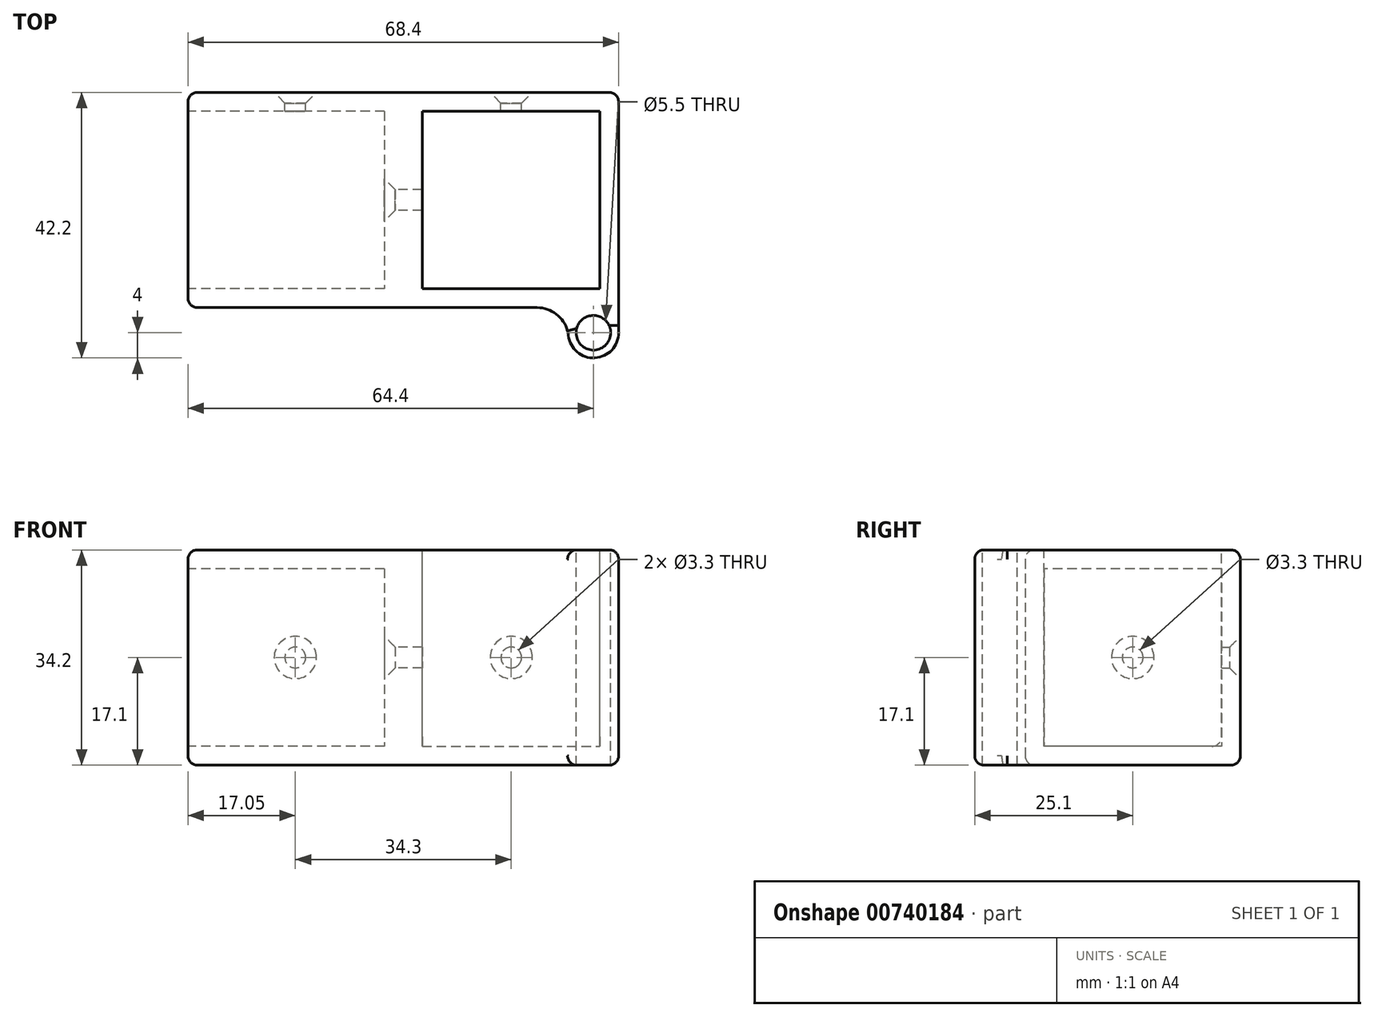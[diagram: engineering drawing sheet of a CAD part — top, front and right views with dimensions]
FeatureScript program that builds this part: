
annotation { "Feature Type Name" : "Feature", "Feature Type Description" : "" }
export const myFeature = defineFeature(function(context is Context, id is Id, definition is map)
    precondition{}
    {
        {
            var Q0;
            Q0=qCreatedBy(makeId("Top.planeOp"),FACE);
            var sketch = newSketch(context, id + "F0", { "sketchPlane" : qUnion([Q0])});
            skLineSegment(sketch, "E0.bottom", {"start": v(-8, 0) * mm, "end": v(-34.2, 0) * mm});
            skLineSegment(sketch, "E0.top", {"start": v(0, 34.2) * mm, "end": v(-34.2, 34.2) * mm});
            skLineSegment(sketch, "E0.left", {"start": v(0, 0) * mm, "end": v(0, 34.2) * mm});
            skLineSegment(sketch, "E0.right", {"start": v(-34.2, 0) * mm, "end": v(-34.2, 34.2) * mm});
            skArc(sketch, "E1", {"start": v(-8, -4) * mm, "mid": v(-4, -8) * mm, "end": v(0, -4) * mm});
            skLineSegment(sketch, "E2", {"start": v(0, 0) * mm, "end": v(0, -4) * mm});
            skLineSegment(sketch, "E3", {"start": v(-8, 0) * mm, "end": v(-8, -4) * mm});
            skLineSegment(sketch, "E4", {"start": v(0, 0) * mm, "end": v(-8, 0) * mm});
            skSolve(sketch);
        }
        {
            var Q0;
            Q0=makeQuery(id+"F0.imprint","IMPRINT",FACE,{"disambiguationData":[TD([[makeQuery(id+"F0.imprint","IMPRINT",EDGE,{"derivedFrom":sQuery(id+"F0.wireOp",EDGE,"E0.bottom")}),-1.0]])]});
            var Q1;
            Q1=makeQuery(id+"F0.imprint","IMPRINT",FACE,{"disambiguationData":[TD([[makeQuery(id+"F0.imprint","IMPRINT",EDGE,{"derivedFrom":sQuery(id+"F0.wireOp",EDGE,"E1")}),1.0]])]});
            extrude(context, id + "F1", {"entities" : qUnion([Q0, Q1]), "depth" : 34.2 * mm, "offsetDistance" : 25 * mm});
        }
        {
            var Q0;
            Q0=makeQuery(id+"F1.opExtrude","CAP_FACE",FACE,{"disambiguationData":[OSD([sQuery(id+"F0.wireOp",EDGE,"E0.bottom"),sQuery(id+"F0.wireOp",EDGE,"E0.top"),sQuery(id+"F0.wireOp",EDGE,"E0.left"),sQuery(id+"F0.wireOp",EDGE,"E0.right"),sQuery(id+"F0.wireOp",EDGE,"E1"),sQuery(id+"F0.wireOp",EDGE,"6FfksXsB-Y7vq-xAn0-bQFg-GBrETYwM94Cl"),sQuery(id+"F0.wireOp",EDGE,"E2"),sQuery(id+"F0.wireOp",EDGE,"E3")])],"isStart":false});
            var sketch = newSketch(context, id + "F2", { "sketchPlane" : qUnion([Q0])});
            skLineSegment(sketch, "E5.bottom", {"start": v(-34.2, 34.2) * mm, "end": v(0, 34.2) * mm});
            skLineSegment(sketch, "E5.top", {"start": v(-34.2, 0) * mm, "end": v(0, 0) * mm});
            skLineSegment(sketch, "E5.left", {"start": v(-34.2, 34.2) * mm, "end": v(-34.2, 0) * mm});
            skLineSegment(sketch, "E5.right", {"start": v(0, 34.2) * mm, "end": v(0, 0) * mm});
            skLineSegment(sketch, "E6.0", {"start": v(-31.2, 31.2) * mm, "end": v(-3, 31.2) * mm});
            skLineSegment(sketch, "E6.1", {"start": v(-31.2, 31.2) * mm, "end": v(-31.2, 3) * mm});
            skLineSegment(sketch, "E6.2", {"start": v(-31.2, 3) * mm, "end": v(-3, 3) * mm});
            skLineSegment(sketch, "E6.3", {"start": v(-3, 31.2) * mm, "end": v(-3, 3) * mm});
            skSolve(sketch);
        }
        {
            var Q0;
            Q0=makeQuery(id+"F2.imprint","IMPRINT",FACE,{"disambiguationData":[TD([[makeQuery(id+"F2.imprint","IMPRINT",EDGE,{"derivedFrom":sQuery(id+"F2.wireOp",EDGE,"E6.0")}),-1.0]])]});
            extrude(context, id + "F3", {"entities" : qUnion([Q0]), "operationType" : NewBodyOperationType.REMOVE, "oppositeDirection" : true, "depth" : 31.2 * mm, "offsetDistance" : 25 * mm});
        }
        {
            var Q0;
            Q0=makeQuery(id+"F1.opExtrude","SWEPT_FACE",FACE,{"disambiguationData":[OSD([sQuery(id+"F0.wireOp",EDGE,"E0.right")])]});
            var sketch = newSketch(context, id + "F4", { "sketchPlane" : qUnion([Q0])});
            skLineSegment(sketch, "E7.bottom", {"start": v(-34.2, 0) * mm, "end": v(0, 0) * mm});
            skLineSegment(sketch, "E7.top", {"start": v(-34.2, 34.2) * mm, "end": v(0, 34.2) * mm});
            skLineSegment(sketch, "E7.left", {"start": v(-34.2, 0) * mm, "end": v(-34.2, 34.2) * mm});
            skLineSegment(sketch, "E7.right", {"start": v(0, 0) * mm, "end": v(0, 34.2) * mm});
            skSolve(sketch);
        }
        {
            var Q0;
            Q0 = qSketchRegion(id + "F4", true);
            extrude(context, id + "F5", {"entities" : qUnion([Q0]), "operationType" : NewBodyOperationType.ADD, "depth" : 34.2 * mm, "offsetDistance" : 25 * mm});
        }
        {
            var Q0;
            Q0=makeQuery(id+"F5.opExtrude","CAP_FACE",FACE,{"disambiguationData":[OSD([sQuery(id+"F4.wireOp",EDGE,"E7.bottom"),sQuery(id+"F4.wireOp",EDGE,"E7.top"),sQuery(id+"F4.wireOp",EDGE,"E7.left"),sQuery(id+"F4.wireOp",EDGE,"E7.right")])],"isStart":false});
            var sketch = newSketch(context, id + "F6", { "sketchPlane" : qUnion([Q0])});
            skLineSegment(sketch, "E8.bottom", {"start": v(-34.2, 34.2) * mm, "end": v(0, 34.2) * mm});
            skLineSegment(sketch, "E8.top", {"start": v(-34.2, 0) * mm, "end": v(0, 0) * mm});
            skLineSegment(sketch, "E8.left", {"start": v(-34.2, 34.2) * mm, "end": v(-34.2, 0) * mm});
            skLineSegment(sketch, "E8.right", {"start": v(0, 34.2) * mm, "end": v(0, 0) * mm});
            skLineSegment(sketch, "E9.0", {"start": v(-31.2, 31.2) * mm, "end": v(-3, 31.2) * mm});
            skLineSegment(sketch, "E9.1", {"start": v(-31.2, 31.2) * mm, "end": v(-31.2, 3) * mm});
            skLineSegment(sketch, "E9.2", {"start": v(-31.2, 3) * mm, "end": v(-3, 3) * mm});
            skLineSegment(sketch, "E9.3", {"start": v(-3, 31.2) * mm, "end": v(-3, 3) * mm});
            skSolve(sketch);
        }
        {
            var Q0;
            Q0=makeQuery(id+"F6.imprint","IMPRINT",FACE,{"disambiguationData":[TD([[makeQuery(id+"F6.imprint","IMPRINT",EDGE,{"derivedFrom":sQuery(id+"F6.wireOp",EDGE,"E9.0")}),-1.0]])]});
            extrude(context, id + "F7", {"entities" : qUnion([Q0]), "operationType" : NewBodyOperationType.REMOVE, "oppositeDirection" : true, "depth" : 31.2 * mm, "offsetDistance" : 25 * mm});
        }
        {
            var Q0;
            Q0=makeQuery(id+"F5.boolean.opBoolean","MERGE",FACE,{"derivedFrom":[makeQuery(id+"F1.opExtrude","SWEPT_FACE",FACE,{"disambiguationData":[OSD([sQuery(id+"F0.wireOp",EDGE,"E0.top")])]}),makeQuery(id+"F5.opExtrude","SWEPT_FACE",FACE,{"disambiguationData":[OSD([sQuery(id+"F4.wireOp",EDGE,"E7.left")])]})]});
            var sketch = newSketch(context, id + "F8", { "sketchPlane" : qUnion([Q0])});
            skPoint(sketch, "E10", {"position": v(17.05, 17.1) * mm});
            skPoint(sketch, "E11", {"position": v(51.35, 17.1) * mm});
            skSolve(sketch);
        }
        {
            var Q0;
            Q0=makeQuery(id+"F7.boolean.opBoolean","COPY",FACE,{"derivedFrom":makeQuery(id+"F7.opExtrude","CAP_FACE",FACE,{"disambiguationData":[OSD([sQuery(id+"F6.wireOp",EDGE,"E9.0"),sQuery(id+"F6.wireOp",EDGE,"E9.1"),sQuery(id+"F6.wireOp",EDGE,"E9.2"),sQuery(id+"F6.wireOp",EDGE,"E9.3")])],"isStart":false})});
            var sketch = newSketch(context, id + "F9", { "sketchPlane" : qUnion([Q0])});
            skPoint(sketch, "E12", {"position": v(-17.1, 17.1) * mm});
            skSolve(sketch);
        }
        {
            var Q0;
            Q0=sQuery(id+"F8.wireOp",VERTEX,"E10");
            var Q1;
            Q1=sQuery(id+"F8.wireOp",VERTEX,"E11");
            var Q2;
            Q2=sQuery(id+"F9.wireOp",VERTEX,"E12");
            var Q3;
            Q3=makeQuery(id+"F1.opExtrude","SWEPT_BODY",BODY,{"disambiguationData":[OSD([sQuery(id+"F0.wireOp",EDGE,"E0.bottom"),sQuery(id+"F0.wireOp",EDGE,"E0.top"),sQuery(id+"F0.wireOp",EDGE,"E0.left"),sQuery(id+"F0.wireOp",EDGE,"E0.right"),sQuery(id+"F0.wireOp",EDGE,"E1"),sQuery(id+"F0.wireOp",EDGE,"6FfksXsB-Y7vq-xAn0-bQFg-GBrETYwM94Cl"),sQuery(id+"F0.wireOp",EDGE,"E2"),sQuery(id+"F0.wireOp",EDGE,"E3")])]});
            hole(context, id + "F10", {"style" : HoleStyle.C_SINK, "endStyle" : HoleEndStyle.BLIND, "standardTappedOrClearance" : lookupTablePath({ "standard" : "ISO", "fit" : "Normal", "size" : "M3", "type" : "Clearance" }), "standardBlindInLast" : lookupTablePath({ "fit" : "Standard", "standard" : "ISO", "size" : "M3", "type" : "Clearance" }), "holeDiameter" : 3.3 * mm, "cSinkDiameter" : 6.72 * mm, "cSinkAngle" : 90 * degree, "majorDiameter" : 5 * mm, "holeDepth" : 25 * mm, "isTappedThrough" : true, "tappedDepth" : 12 * mm, "tapClearance" : 3, "startFromSketch" : true, "locations" : qUnion([Q0, Q1, Q2]), "scope" : qUnion([Q3])});
        }
        {
            var Q0;
            Q0=makeQuery(id+"F5.boolean.opBoolean","MERGE",FACE,{"derivedFrom":[makeQuery(id+"F1.opExtrude","CAP_FACE",FACE,{"disambiguationData":[OSD([sQuery(id+"F0.wireOp",EDGE,"E0.bottom"),sQuery(id+"F0.wireOp",EDGE,"E0.top"),sQuery(id+"F0.wireOp",EDGE,"E0.left"),sQuery(id+"F0.wireOp",EDGE,"E0.right"),sQuery(id+"F0.wireOp",EDGE,"E1"),sQuery(id+"F0.wireOp",EDGE,"E2"),sQuery(id+"F0.wireOp",EDGE,"E3")])],"isStart":false}),makeQuery(id+"F5.opExtrude","SWEPT_FACE",FACE,{"disambiguationData":[OSD([sQuery(id+"F4.wireOp",EDGE,"E7.top")])]})]});
            var sketch = newSketch(context, id + "F11", { "sketchPlane" : qUnion([Q0])});
            skPoint(sketch, "E13", {"position": v(-4, -4) * mm});
            skSolve(sketch);
        }
        {
            var Q0;
            Q0=sQuery(id+"F11.wireOp",VERTEX,"E13");
            var Q1;
            Q1=makeQuery(id+"F1.opExtrude","SWEPT_BODY",BODY,{"disambiguationData":[OSD([sQuery(id+"F0.wireOp",EDGE,"E0.bottom"),sQuery(id+"F0.wireOp",EDGE,"E0.top"),sQuery(id+"F0.wireOp",EDGE,"E0.left"),sQuery(id+"F0.wireOp",EDGE,"E0.right"),sQuery(id+"F0.wireOp",EDGE,"E1"),sQuery(id+"F0.wireOp",EDGE,"E2"),sQuery(id+"F0.wireOp",EDGE,"E3")])]});
            hole(context, id + "F12", {"style" : HoleStyle.SIMPLE, "endStyle" : HoleEndStyle.THROUGH, "standardTappedOrClearance" : lookupTablePath({ "standard" : "ISO", "fit" : "Normal", "size" : "M5", "type" : "Clearance" }), "standardBlindInLast" : lookupTablePath({ "fit" : "Standard", "standard" : "ISO", "size" : "M5", "type" : "Clearance" }), "holeDiameter" : 5.5 * mm, "majorDiameter" : 5 * mm, "isTappedThrough" : true, "tappedDepth" : 12 * mm, "tapClearance" : 3, "startFromSketch" : true, "locations" : qUnion([Q0]), "scope" : qUnion([Q1])});
        }
        {
            var Q0;
            Q0=makeQuery(id+"F1.opExtrude","SWEPT_EDGE",EDGE,{"disambiguationData":[OSD([sQuery(id+"F0.wireOp",EDGE,"E0.bottom"),sQuery(id+"F0.wireOp",EDGE,"E3"),sQuery(id+"F0.wireOp",EDGE,"E4")])]});
            fillet(context, id + "F13", {"entities" : qUnion([Q0]), "radius" : 5 * mm, "tangentPropagation" : true, "allowEdgeOverflow" : false});
        }
        {
            var Q0;
            Q0=makeQuery(id+"F3.boolean.opBoolean","COPY",EDGE,{"derivedFrom":makeQuery(id+"F3.opExtrude","CAP_EDGE",EDGE,{"disambiguationData":[OSD([sQuery(id+"F2.wireOp",EDGE,"E6.2")])],"isStart":true})});
            var Q1;
            Q1=makeQuery(id+"F3.boolean.opBoolean","COPY",EDGE,{"derivedFrom":makeQuery(id+"F3.opExtrude","CAP_EDGE",EDGE,{"disambiguationData":[OSD([sQuery(id+"F2.wireOp",EDGE,"E6.1")])],"isStart":true})});
            var Q2;
            Q2=makeQuery(id+"F3.boolean.opBoolean","COPY",EDGE,{"derivedFrom":makeQuery(id+"F3.opExtrude","CAP_EDGE",EDGE,{"disambiguationData":[OSD([sQuery(id+"F2.wireOp",EDGE,"E6.0")])],"isStart":true})});
            var Q3;
            Q3=makeQuery(id+"F3.boolean.opBoolean","COPY",EDGE,{"derivedFrom":makeQuery(id+"F3.opExtrude","CAP_EDGE",EDGE,{"disambiguationData":[OSD([sQuery(id+"F2.wireOp",EDGE,"E6.0")])],"isStart":false})});
            var Q4;
            Q4=makeQuery(id+"F1.opExtrude","CAP_EDGE",EDGE,{"disambiguationData":[OSD([sQuery(id+"F0.wireOp",EDGE,"E0.left"),sQuery(id+"F0.wireOp",EDGE,"E2")])],"isStart":false});
            var Q5;
            Q5=makeQuery(id+"F5.boolean.opBoolean","MERGE",EDGE,{"derivedFrom":[makeQuery(id+"F1.opExtrude","CAP_EDGE",EDGE,{"disambiguationData":[OSD([sQuery(id+"F0.wireOp",EDGE,"E0.bottom")])],"isStart":false}),makeQuery(id+"F5.opExtrude","SWEPT_EDGE",EDGE,{"disambiguationData":[OSD([sQuery(id+"F4.wireOp",EDGE,"E7.top"),sQuery(id+"F4.wireOp",EDGE,"E7.right")])]})]});
            var Q6;
            Q6=makeQuery(id+"F5.opExtrude","CAP_EDGE",EDGE,{"disambiguationData":[OSD([sQuery(id+"F4.wireOp",EDGE,"E7.top")])],"isStart":false});
            var Q7;
            Q7=makeQuery(id+"F5.boolean.opBoolean","MERGE",EDGE,{"derivedFrom":[makeQuery(id+"F1.opExtrude","CAP_EDGE",EDGE,{"disambiguationData":[OSD([sQuery(id+"F0.wireOp",EDGE,"E0.top")])],"isStart":false}),makeQuery(id+"F5.opExtrude","SWEPT_EDGE",EDGE,{"disambiguationData":[OSD([sQuery(id+"F4.wireOp",EDGE,"E7.top"),sQuery(id+"F4.wireOp",EDGE,"E7.left")])]})]});
            var Q8;
            Q8=makeQuery(id+"F1.opExtrude","SWEPT_EDGE",EDGE,{"disambiguationData":[OSD([sQuery(id+"F0.wireOp",EDGE,"E0.top"),sQuery(id+"F0.wireOp",EDGE,"E0.left")])]});
            var Q9;
            Q9=makeQuery(id+"F7.boolean.opBoolean","COPY",EDGE,{"derivedFrom":makeQuery(id+"F7.opExtrude","CAP_EDGE",EDGE,{"disambiguationData":[OSD([sQuery(id+"F6.wireOp",EDGE,"E9.0")])],"isStart":true})});
            var Q10;
            Q10=makeQuery(id+"F5.opExtrude","CAP_EDGE",EDGE,{"disambiguationData":[OSD([sQuery(id+"F4.wireOp",EDGE,"E7.right")])],"isStart":false});
            var Q11;
            Q11=makeQuery(id+"F7.boolean.opBoolean","COPY",EDGE,{"derivedFrom":makeQuery(id+"F7.opExtrude","CAP_EDGE",EDGE,{"disambiguationData":[OSD([sQuery(id+"F6.wireOp",EDGE,"E9.3")])],"isStart":true})});
            var Q12;
            Q12=makeQuery(id+"F7.boolean.opBoolean","COPY",EDGE,{"derivedFrom":makeQuery(id+"F7.opExtrude","CAP_EDGE",EDGE,{"disambiguationData":[OSD([sQuery(id+"F6.wireOp",EDGE,"E9.1")])],"isStart":true})});
            var Q13;
            Q13=makeQuery(id+"F5.opExtrude","CAP_EDGE",EDGE,{"disambiguationData":[OSD([sQuery(id+"F4.wireOp",EDGE,"E7.left")])],"isStart":false});
            var Q14;
            Q14=makeQuery(id+"F7.boolean.opBoolean","COPY",EDGE,{"derivedFrom":makeQuery(id+"F7.opExtrude","CAP_EDGE",EDGE,{"disambiguationData":[OSD([sQuery(id+"F6.wireOp",EDGE,"E9.2")])],"isStart":true})});
            var Q15;
            Q15=makeQuery(id+"F5.opExtrude","CAP_EDGE",EDGE,{"disambiguationData":[OSD([sQuery(id+"F4.wireOp",EDGE,"E7.bottom")])],"isStart":false});
            var Q16;
            Q16=makeQuery(id+"F5.boolean.opBoolean","MERGE",EDGE,{"derivedFrom":[makeQuery(id+"F1.opExtrude","CAP_EDGE",EDGE,{"disambiguationData":[OSD([sQuery(id+"F0.wireOp",EDGE,"E0.bottom")])],"isStart":true}),makeQuery(id+"F5.opExtrude","SWEPT_EDGE",EDGE,{"disambiguationData":[OSD([sQuery(id+"F4.wireOp",EDGE,"E7.bottom"),sQuery(id+"F4.wireOp",EDGE,"E7.right")])]})]});
            var Q17;
            Q17=makeQuery(id+"F5.boolean.opBoolean","MERGE",EDGE,{"derivedFrom":[makeQuery(id+"F1.opExtrude","CAP_EDGE",EDGE,{"disambiguationData":[OSD([sQuery(id+"F0.wireOp",EDGE,"E0.top")])],"isStart":true}),makeQuery(id+"F5.opExtrude","SWEPT_EDGE",EDGE,{"disambiguationData":[OSD([sQuery(id+"F4.wireOp",EDGE,"E7.bottom"),sQuery(id+"F4.wireOp",EDGE,"E7.left")])]})]});
            fillet(context, id + "F14", {"entities" : qUnion([Q0, Q1, Q2, Q3, Q4, Q5, Q6, Q7, Q8, Q9, Q10, Q11, Q12, Q13, Q14, Q15, Q16, Q17]), "radius" : 1.5 * mm, "tangentPropagation" : true, "allowEdgeOverflow" : false});
        }
    });
